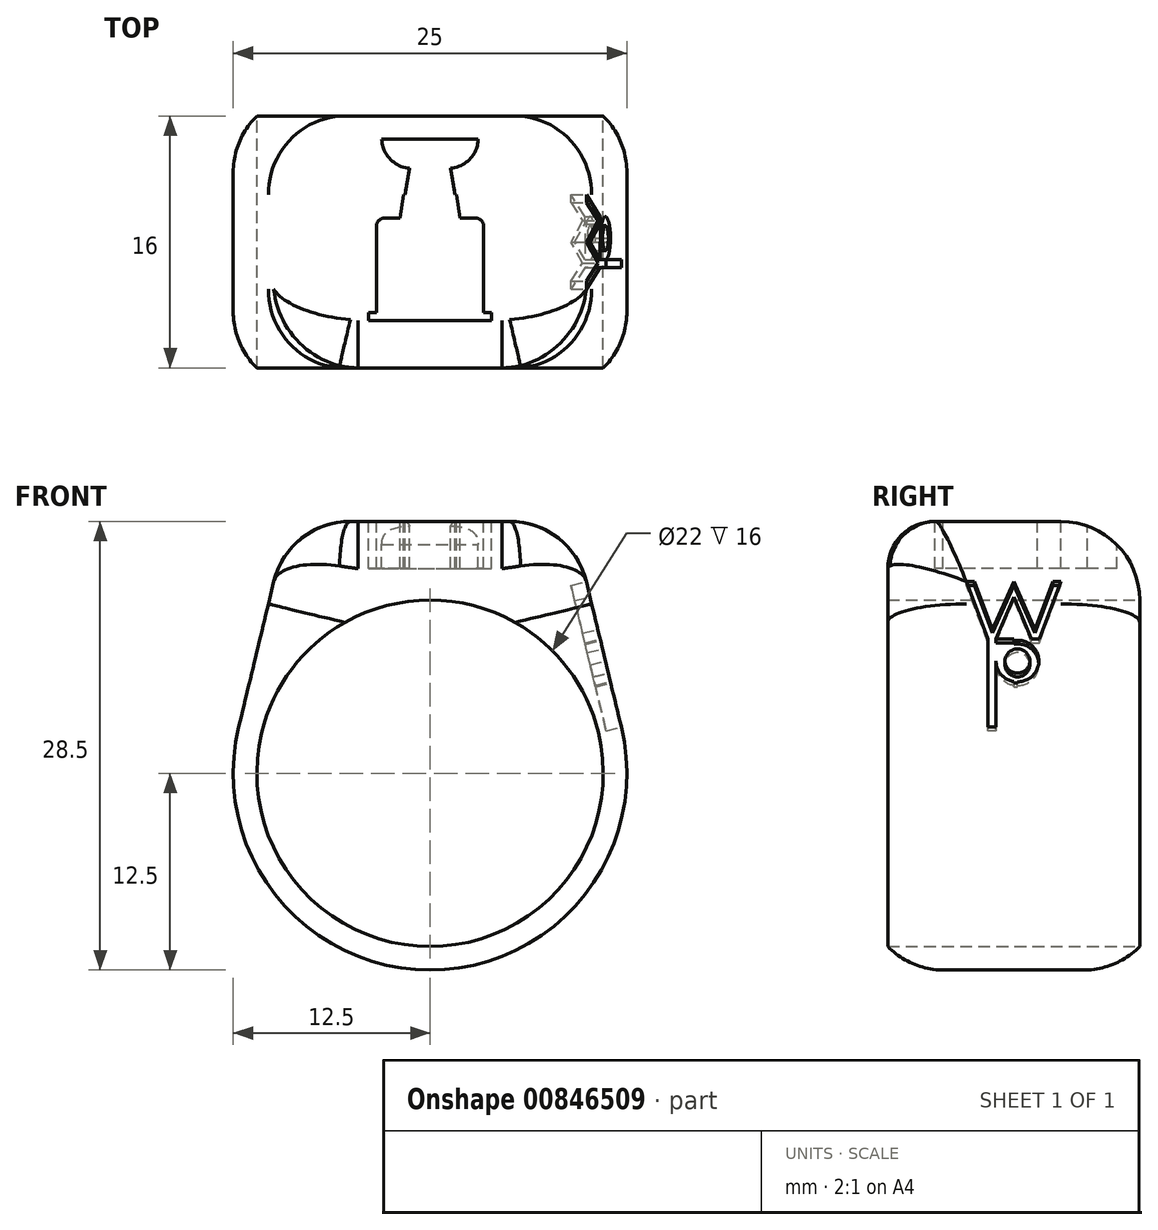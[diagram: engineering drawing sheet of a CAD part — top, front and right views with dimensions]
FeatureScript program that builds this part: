
annotation { "Feature Type Name" : "Feature", "Feature Type Description" : "" }
export const myFeature = defineFeature(function(context is Context, id is Id, definition is map)
    precondition{}
    {
        {
            var Q0;
            Q0=qCreatedBy(makeId("Front.planeOp"),FACE);
            var sketch = newSketch(context, id + "F0", { "sketchPlane" : qUnion([Q0])});
            skCircle(sketch, "E0", {"center": v(0, 0) * mm, "radius": 11 * mm});
            skArc(sketch, "E1", {"start": v(-3.5, 12) * mm, "mid": v(0, -12.5) * mm, "end": v(3.5, 12) * mm});
            skLineSegment(sketch, "E2", {"start": v(-3.5, 12) * mm, "end": v(3.5, 12) * mm});
            skPoint(sketch, "E3.orphan", {"position": v(12.9, 17) * mm});
            skPoint(sketch, "E4.end.orphan", {"position": v(12.9, 11) * mm});
            skSolve(sketch);
        }
        {
            var Q0;
            Q0=qSketchRegion(id+"F0",true);
            extrude(context, id + "F1", {"entities" : qUnion([Q0]), "depth" : 16 * mm, "offsetDistance" : 25 * mm});
        }
        {
            var Q0;
            Q0=makeQuery(id+"F1.opExtrude","SWEPT_FACE",FACE,{"disambiguationData":[OSD([sQuery(id+"F0.wireOp",EDGE,"E2")])]});
            var sketch = newSketch(context, id + "F2", { "sketchPlane" : qUnion([Q0])});
            skLineSegment(sketch, "E5", {"start": v(-9, 0) * mm, "end": v(-9, -16) * mm});
            skLineSegment(sketch, "E6", {"start": v(-9, -16) * mm, "end": v(9, -16) * mm});
            skLineSegment(sketch, "E7", {"start": v(9, -16) * mm, "end": v(9, 0) * mm});
            skLineSegment(sketch, "E8", {"start": v(9, 0) * mm, "end": v(-9, 0) * mm});
            skSolve(sketch);
        }
        {
            var Q0;
            Q0=qSketchRegion(id+"F2",true);
            extrude(context, id + "F3", {"entities" : qUnion([Q0]), "operationType" : NewBodyOperationType.ADD, "depth" : 4 * mm, "offsetDistance" : 25 * mm});
        }
        {
            var Q0;
            Q0=makeQuery(id+"F3.boolean.opBoolean","MERGE",FACE,{"derivedFrom":[makeQuery(id+"F1.opExtrude","CAP_FACE",FACE,{"disambiguationData":[OSD([sQuery(id+"F0.wireOp",EDGE,"E0"),sQuery(id+"F0.wireOp",EDGE,"E1"),sQuery(id+"F0.wireOp",EDGE,"E2")])],"isStart":false}),makeQuery(id+"F3.opExtrude","SWEPT_FACE",FACE,{"disambiguationData":[OSD([sQuery(id+"F2.wireOp",EDGE,"E6")])]})]});
            var sketch = newSketch(context, id + "F4", { "sketchPlane" : qUnion([Q0])});
            skLineSegment(sketch, "E9", {"start": v(-9, 12) * mm, "end": v(-9, 8.67) * mm});
            skLineSegment(sketch, "E10", {"start": v(9, 12) * mm, "end": v(9, 8.68) * mm});
            skSolve(sketch);
        }
        {
            var Q0;
            Q0=qSketchRegion(id+"F4",true);
            var Q1;
            {var subQ0=sQuery(id+"F4.wireOp",EDGE,"E9");Q1=makeQuery(id+"F4.imprint","IMPRINT",FACE,{"disambiguationData":[TD([[makeQuery(id+"F4.imprint","IMPRINT",EDGE,{"derivedFrom":subQ0}),1.0]])]});}
            var Q2;
            {var subQ0=sQuery(id+"F4.wireOp",EDGE,"E10");Q2=makeQuery(id+"F4.imprint","IMPRINT",FACE,{"disambiguationData":[TD([[makeQuery(id+"F4.imprint","IMPRINT",EDGE,{"derivedFrom":subQ0}),-1.0]])]});}
            extrude(context, id + "F5", {"entities" : qUnion([Q0, Q1, Q2]), "operationType" : NewBodyOperationType.ADD, "oppositeDirection" : true, "depth" : 16 * mm, "offsetDistance" : 25 * mm});
        }
        {
            var Q0;
            {var subQ0=sQuery(id+"F2.wireOp",EDGE,"E6");var subQ1=sQuery(id+"F0.wireOp",EDGE,"E1");Q0=makeQuery(id+"F5.boolean.opBoolean","MERGE",FACE,{"derivedFrom":[makeQuery(id+"F3.boolean.opBoolean","MERGE",FACE,{"derivedFrom":[makeQuery(id+"F1.opExtrude","CAP_FACE",FACE,{"disambiguationData":[OSD([sQuery(id+"F0.wireOp",EDGE,"E0"),subQ1,sQuery(id+"F0.wireOp",EDGE,"E2")])],"isStart":false}),makeQuery(id+"F3.opExtrude","SWEPT_FACE",FACE,{"disambiguationData":[OSD([subQ0])]})]}),makeQuery(id+"F5.opExtrude","CAP_FACE",FACE,{"disambiguationData":[OSD([subQ1,subQ0,sQuery(id+"F4.wireOp",EDGE,"E9")])],"isStart":true}),makeQuery(id+"F5.opExtrude","CAP_FACE",FACE,{"disambiguationData":[OSD([subQ1,subQ0,sQuery(id+"F4.wireOp",EDGE,"E10")])],"isStart":true})]});}
            var sketch = newSketch(context, id + "F6", { "sketchPlane" : qUnion([Q0])});
            skLineSegment(sketch, "E11", {"start": v(-9, 16) * mm, "end": v(-12.15, 2.93) * mm});
            skLineSegment(sketch, "E12", {"start": v(9, 16) * mm, "end": v(12.15, 2.93) * mm});
            skSolve(sketch);
        }
        {
            var Q0;
            Q0=qSketchRegion(id+"F6",true);
            var Q1;
            {var subQ0=sQuery(id+"F6.wireOp",EDGE,"E11");Q1=makeQuery(id+"F6.imprint","IMPRINT",FACE,{"disambiguationData":[TD([[makeQuery(id+"F6.imprint","IMPRINT",EDGE,{"derivedFrom":subQ0}),1.0]])]});}
            var Q2;
            {var subQ0=sQuery(id+"F6.wireOp",EDGE,"E12");Q2=makeQuery(id+"F6.imprint","IMPRINT",FACE,{"disambiguationData":[TD([[makeQuery(id+"F6.imprint","IMPRINT",EDGE,{"derivedFrom":subQ0}),-1.0]])]});}
            extrude(context, id + "F7", {"entities" : qUnion([Q0, Q1, Q2]), "operationType" : NewBodyOperationType.ADD, "oppositeDirection" : true, "depth" : 16 * mm, "offsetDistance" : 25 * mm});
        }
        {
            var Q0;
            Q0=makeQuery(id+"F3.opExtrude","CAP_EDGE",EDGE,{"disambiguationData":[OSD([sQuery(id+"F2.wireOp",EDGE,"E6")])],"isStart":false});
            fillet(context, id + "F8", {"entities" : qUnion([Q0]), "radius" : 3 * mm, "tangentPropagation" : true, "allowEdgeOverflow" : false});
        }
        {
            var Q0;
            {var subQ0=sQuery(id+"F2.wireOp",EDGE,"E7");Q0=makeQuery(id+"F7.boolean.opBoolean","MERGE",EDGE,{"derivedFrom":[makeQuery(id+"F3.opExtrude","CAP_EDGE",EDGE,{"disambiguationData":[OSD([subQ0])],"isStart":false}),makeQuery(id+"F7.opExtrude","SWEPT_EDGE",EDGE,{"disambiguationData":[OSD([sQuery(id+"F2.wireOp",EDGE,"E6"),subQ0,sQuery(id+"F4.wireOp",EDGE,"E10"),sQuery(id+"F6.wireOp",EDGE,"E12")])]})]});}
            var Q1;
            Q1=makeQuery(id+"F3.opExtrude","CAP_EDGE",EDGE,{"disambiguationData":[OSD([sQuery(id+"F2.wireOp",EDGE,"E8")])],"isStart":false});
            fillet(context, id + "F9", {"entities" : qUnion([Q0, Q1]), "radius" : 5 * mm, "tangentPropagation" : true, "allowEdgeOverflow" : false});
        }
        {
            var Q0;
            {var subQ0=sQuery(id+"F2.wireOp",EDGE,"E5");Q0=makeQuery(id+"F9.opFillet","BLEND_EDGE",EDGE,{"blendedFrom":[makeQuery(id+"F3.opExtrude","CAP_EDGE",EDGE,{"disambiguationData":[OSD([sQuery(id+"F2.wireOp",EDGE,"E8")])],"isStart":false}),makeQuery(id+"F7.boolean.opBoolean","MERGE",EDGE,{"derivedFrom":[makeQuery(id+"F3.opExtrude","CAP_EDGE",EDGE,{"disambiguationData":[OSD([subQ0])],"isStart":false}),makeQuery(id+"F7.opExtrude","SWEPT_EDGE",EDGE,{"disambiguationData":[OSD([subQ0,sQuery(id+"F2.wireOp",EDGE,"E6"),sQuery(id+"F4.wireOp",EDGE,"E9"),sQuery(id+"F6.wireOp",EDGE,"E11")])]})]})],"blendedInto":[]});}
            fillet(context, id + "F10", {"entities" : qUnion([Q0]), "radius" : 5 * mm, "tangentPropagation" : true, "allowEdgeOverflow" : false});
        }
        {
            var Q0;
            Q0=makeQuery(id+"F3.opExtrude","CAP_FACE",FACE,{"disambiguationData":[OSD([sQuery(id+"F2.wireOp",EDGE,"E5"),sQuery(id+"F2.wireOp",EDGE,"E6"),sQuery(id+"F2.wireOp",EDGE,"E7"),sQuery(id+"F2.wireOp",EDGE,"E8")])],"isStart":false});
            var sketch = newSketch(context, id + "F11", { "sketchPlane" : qUnion([Q0])});
            skLineSegment(sketch, "E13", {"start": v(-3.06, -1.46) * mm, "end": v(3.06, -1.46) * mm});
            skArc(sketch, "E14", {"start": v(-3.06, -1.46) * mm, "mid": v(-2.54, -2.73) * mm, "end": v(-1.3, -3.32) * mm});
            skArc(sketch, "E15", {"start": v(1.3, -3.32) * mm, "mid": v(2.54, -2.73) * mm, "end": v(3.06, -1.46) * mm});
            skLineSegment(sketch, "E16", {"start": v(-1.3, -3.32) * mm, "end": v(-1.6, -5) * mm});
            skLineSegment(sketch, "E17", {"start": v(1.3, -3.32) * mm, "end": v(1.6, -5) * mm});
            skLineSegment(sketch, "E18", {"start": v(-1.6, -5) * mm, "end": v(-1.7, -5) * mm});
            skLineSegment(sketch, "E19", {"start": v(1.6, -5) * mm, "end": v(1.7, -5) * mm});
            skLineSegment(sketch, "E20", {"start": v(-1.7, -5) * mm, "end": v(-1.9, -6.49) * mm});
            skLineSegment(sketch, "E21", {"start": v(1.7, -5) * mm, "end": v(1.9, -6.49) * mm});
            skLineSegment(sketch, "E22", {"start": v(-1.9, -6.49) * mm, "end": v(-2.9, -6.49) * mm});
            skLineSegment(sketch, "E23", {"start": v(1.9, -6.49) * mm, "end": v(2.9, -6.49) * mm});
            skLineSegment(sketch, "E24", {"start": v(-3.4, -6.99) * mm, "end": v(-3.4, -12.49) * mm});
            skLineSegment(sketch, "E25", {"start": v(3.4, -6.99) * mm, "end": v(3.4, -12.49) * mm});
            skLineSegment(sketch, "E26", {"start": v(3.4, -12.49) * mm, "end": v(3.9, -12.49) * mm});
            skLineSegment(sketch, "E27", {"start": v(-3.4, -12.49) * mm, "end": v(-3.9, -12.49) * mm});
            skLineSegment(sketch, "E28", {"start": v(-3.9, -12.49) * mm, "end": v(-3.9, -13) * mm});
            skLineSegment(sketch, "E29", {"start": v(-3.9, -13) * mm, "end": v(3.9, -13) * mm});
            skLineSegment(sketch, "E30", {"start": v(3.9, -13) * mm, "end": v(3.9, -12.49) * mm});
            skPoint(sketch, "E31.visualSharp", {"position": v(-3.4, -6.49) * mm});
            skArc(sketch, "E31.filletArc", {"start": v(-2.9, -6.49) * mm, "mid": v(-3.26, -6.63) * mm, "end": v(-3.4, -6.99) * mm});
            skPoint(sketch, "E32.visualSharp", {"position": v(3.4, -6.49) * mm});
            skArc(sketch, "E32.filletArc", {"start": v(3.4, -6.99) * mm, "mid": v(3.26, -6.63) * mm, "end": v(2.9, -6.49) * mm});
            skSolve(sketch);
        }
        {
            var Q0;
            Q0 = qSketchRegion(id + "F11", true);
            extrude(context, id + "F12", {"entities" : qUnion([Q0]), "operationType" : NewBodyOperationType.REMOVE, "oppositeDirection" : true, "depth" : 3 * mm, "offsetDistance" : 25 * mm});
        }
        {
            var Q0;
            Q0=makeQuery(id+"F7.opExtrude","SWEPT_FACE",FACE,{"disambiguationData":[OSD([sQuery(id+"F6.wireOp",EDGE,"E12")])]});
            var sketch = newSketch(context, id + "F13", { "sketchPlane" : qUnion([Q0])});
            skLineSegment(sketch, "E33", {"start": v(-8, 5.75) * mm, "end": v(-4.75, 5.75) * mm});
            skPoint(sketch, "E34.end.orphan", {"position": v(-11, 5.75) * mm});
            skLineSegment(sketch, "E35", {"start": v(-8, 5.75) * mm, "end": v(-11.25, 5.75) * mm});
            skLineSegment(sketch, "E36", {"start": v(-9.62, 5.75) * mm, "end": v(-11, 9.5) * mm});
            skLineSegment(sketch, "E37", {"start": v(-10.5, 9.5) * mm, "end": v(-9.35, 6.38) * mm});
            skLineSegment(sketch, "E38", {"start": v(-6.38, 5.75) * mm, "end": v(-5, 9.5) * mm});
            skLineSegment(sketch, "E39", {"start": v(-5.5, 9.5) * mm, "end": v(-6.65, 6.38) * mm});
            skLineSegment(sketch, "E40", {"start": v(-9.35, 6.38) * mm, "end": v(-8, 9.5) * mm});
            skLineSegment(sketch, "E41", {"start": v(-6.65, 6.38) * mm, "end": v(-8, 9.5) * mm});
            skLineSegment(sketch, "E42", {"start": v(-9.12, 5.75) * mm, "end": v(-8, 8.5) * mm});
            skLineSegment(sketch, "E43", {"start": v(-8, 8.5) * mm, "end": v(-6.88, 5.75) * mm});
            skLineSegment(sketch, "E44", {"start": v(-8, 5.75) * mm, "end": v(-8, 5.66) * mm});
            skLineSegment(sketch, "E45", {"start": v(-9.62, 2.88) * mm, "end": v(-9.62, 0) * mm});
            skLineSegment(sketch, "E46", {"start": v(-9.12, 5.75) * mm, "end": v(-9.12, 4.75) * mm});
            skLineSegment(sketch, "E47", {"start": v(-8, 2.88) * mm, "end": v(-7.76, 2.88) * mm});
            skLineSegment(sketch, "E48", {"start": v(-9.62, 2.88) * mm, "end": v(-9.62, 5.75) * mm});
            skLineSegment(sketch, "E49", {"start": v(-7.76, 2.88) * mm, "end": v(-7.76, 2.95) * mm});
            skCircle(sketch, "E50", {"center": v(-7.76, 4.32) * mm, "radius": 1.36 * mm});
            skPoint(sketch, "E50.centerSnap0", {"position": v(-7.82, 4.32) * mm});
            skCircle(sketch, "E51", {"center": v(-7.76, 4.32) * mm, "radius": 0.8 * mm});
            skPoint(sketch, "E52.trimOffspring.end.orphan", {"position": v(-6.02, 4.32) * mm});
            skLineSegment(sketch, "E53.trimOffspring", {"start": v(-7.82, 4.32) * mm, "end": v(-7.76, 4.32) * mm});
            skLineSegment(sketch, "E54.trimOffspring", {"start": v(-8, 2.98) * mm, "end": v(-8, 2.88) * mm});
            skPoint(sketch, "E55.orphan", {"position": v(-8, 0) * mm});
            skPoint(sketch, "E56.orphan", {"position": v(-9.62, 4.32) * mm});
            skPoint(sketch, "E57.orphan", {"position": v(-5.9, 2.88) * mm});
            skLineSegment(sketch, "E58", {"start": v(-9.12, 4.32) * mm, "end": v(-9.12, 0) * mm});
            skLineSegment(sketch, "E59", {"start": v(-9.12, 0) * mm, "end": v(-9.62, 0) * mm});
            skSolve(sketch);
        }
        {
            var Q0;
            Q0=makeQuery(id+"F13.imprint","IMPRINT",FACE,{"disambiguationData":[TD([[makeQuery(id+"F13.imprint","IMPRINT",EDGE,{"derivedFrom":sQuery(id+"F13.wireOp",EDGE,"E47")}),1.0]])]});
            var Q1;
            Q1=makeQuery(id+"F13.imprint","IMPRINT",FACE,{"disambiguationData":[TD([[makeQuery(id+"F13.imprint","IMPRINT",EDGE,{"derivedFrom":sQuery(id+"F13.wireOp",EDGE,"E51")}),-1.0]])]});
            var Q2;
            {var subQ2=sQuery(id+"F13.wireOp",EDGE,"E44");Q2=makeQuery(id+"F13.imprint","IMPRINT",FACE,{"disambiguationData":[TD([[makeQuery(id+"F13.imprint","IMPRINT",EDGE,{"derivedFrom":subQ2}),-1.0]])]});}
            var Q3;
            {var subQ7=sQuery(id+"F13.wireOp",EDGE,"E36");Q3=makeQuery(id+"F13.imprint","IMPRINT",FACE,{"disambiguationData":[TD([[makeQuery(id+"F13.imprint","IMPRINT",EDGE,{"derivedFrom":subQ7}),-1.0]])]});}
            extrude(context, id + "F14", {"entities" : qUnion([Q0, Q1, Q2, Q3]), "operationType" : NewBodyOperationType.REMOVE, "oppositeDirection" : true, "depth" : 1 * mm, "offsetDistance" : 25 * mm});
        }
    });
